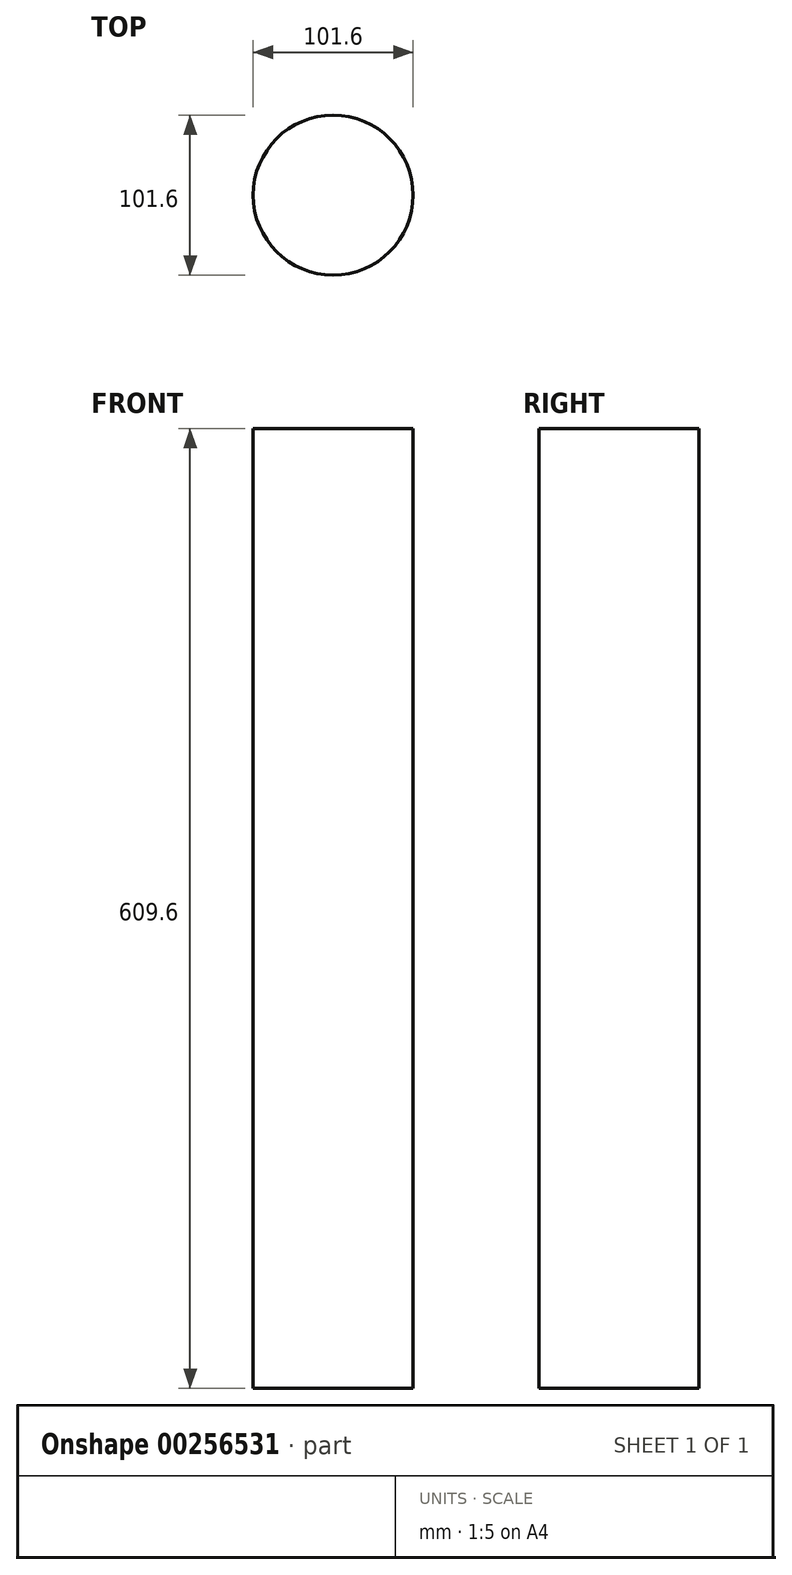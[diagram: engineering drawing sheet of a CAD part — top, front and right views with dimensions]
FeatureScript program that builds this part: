
annotation { "Feature Type Name" : "Feature", "Feature Type Description" : "" }
export const myFeature = defineFeature(function(context is Context, id is Id, definition is map)
    precondition{}
    {
        {
            var Q0;
            Q0=qCreatedBy(makeId("Top.planeOp"),FACE);
            var sketch = newSketch(context, id + "F0", { "sketchPlane" : qUnion([Q0])});
            skCircle(sketch, "E0", {"center": v(0, 0) * mm, "radius": 50.8 * mm});
            skSolve(sketch);
        }
        {
            var Q0;
            Q0 = qSketchRegion(id + "F0", true);
            extrude(context, id + "F1", {"entities" : qUnion([Q0]), "depth" : 609.6 * mm});
        }
    });
